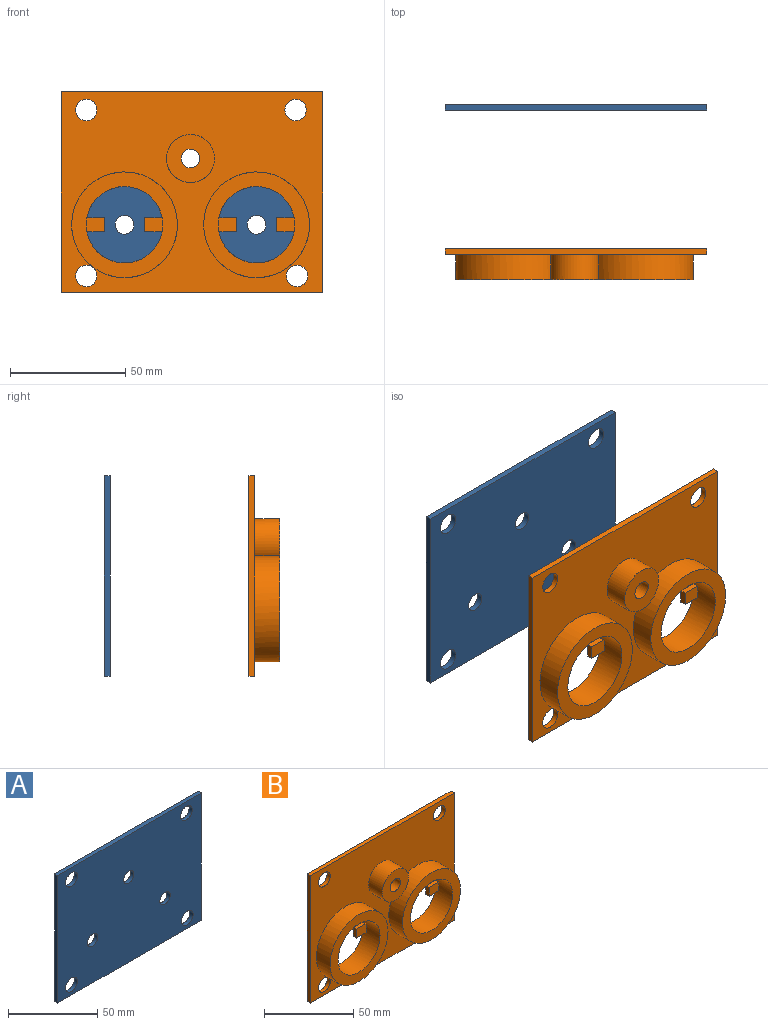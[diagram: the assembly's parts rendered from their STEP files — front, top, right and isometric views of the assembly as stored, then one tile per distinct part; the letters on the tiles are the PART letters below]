
ASSEMBLY  parts=2 mates=1
PART A: 13 faces, bbox 113.6x2.5x87.2 mm
  f0: plane 113.61x2.54mm, normal (0,0,-1), area 288.6mm2, adj f1,f10,f11,f12
  f1: plane 87.22x2.54mm, normal (1,0,0), area 221.5mm2, adj f0,f2,f11,f12
  f2: plane 113.61x2.54mm, normal (0,0,1), area 288.6mm2, adj f1,f10,f11,f12
  f3: cylinder r=4.65mm len=9.29mm, axis (0,1,0), area 74.1mm2, adj f11,f12
  f4: cylinder r=4.65mm len=9.29mm, axis (0,1,0), area 74.1mm2, adj f11,f12
  f5: cylinder r=4.65mm len=9.29mm, axis (0,1,0), area 74.1mm2, adj f11,f12
  f6: cylinder r=4.65mm len=9.29mm, axis (0,1,0), area 74.1mm2, adj f11,f12
  f7: cylinder r=4.07mm len=8.14mm, axis (0,1,0), area 65mm2, adj f11,f12
  f8: cylinder r=4.07mm len=8.14mm, axis (0,1,0), area 65mm2, adj f11,f12
  f9: cylinder r=4.07mm len=8.14mm, axis (0,1,0), area 65mm2, adj f11,f12
  f10: plane 87.22x2.54mm, normal (-1,0,0), area 221.5mm2, adj f0,f2,f11,f12
  f11: plane 113.61x87.22mm, normal (0,-1,0), area 9481.8mm2, adj f0,f1,f2,f3,f4,f5,f6,f7
  f12: plane 113.61x87.22mm, normal (0,1,0), area 9481.8mm2, adj f0,f1,f2,f3,f4,f5,f6,f7
PART B: 35 faces, bbox 113.6x13.3x87.2 mm
  f0: plane 113.61x2.54mm, normal (0,0,1), area 288.6mm2, adj f1,f5,f11,f12
  f1: plane 87.22x2.54mm, normal (-1,0,0), area 221.5mm2, adj f0,f2,f11,f12
  f2: plane 113.61x2.54mm, normal (0,0,-1), area 288.6mm2, adj f1,f5,f11,f12
  f3: cylinder r=4.07mm len=13.34mm, axis (0,1,0), area 341mm2, adj f12,f18
  f4: cylinder r=16.61mm len=33.23mm, axis (0,1,0), area 1360.9mm2, adj f12,f14,f27,f29,f30,f31,f33,f34
  f5: plane 87.22x2.54mm, normal (1,0,0), area 221.5mm2, adj f0,f2,f11,f12
  f6: cylinder r=4.65mm len=9.29mm, axis (0,1,0), area 74.1mm2, adj f11,f12
  f7: cylinder r=4.65mm len=9.29mm, axis (0,1,0), area 74.1mm2, adj f11,f12
  f8: cylinder r=4.65mm len=9.29mm, axis (0,1,0), area 74.1mm2, adj f11,f12
  f9: cylinder r=4.65mm len=9.29mm, axis (0,1,0), area 74.1mm2, adj f11,f12
  f10: cylinder r=16.61mm len=33.23mm, axis (0,1,0), area 1360.9mm2, adj f12,f16,f20,f21,f22,f23,f25,f26
  f11: plane 113.61x87.22mm, normal (0,-1,0), area 5983.5mm2, adj f0,f1,f2,f5,f6,f7,f8,f9
  f12: plane 113.61x87.22mm, normal (0,1,0), area 8038.4mm2, adj f0,f1,f2,f3,f4,f5,f6,f7
  f13: cylinder r=22.96mm len=45.93mm, axis (0,1,0), area 1557.6mm2, adj f11,f14
  f14: plane 45.93x45.93mm, normal (0,-1,0), area 789.5mm2, adj f4,f13
  f15: cylinder r=22.96mm len=45.93mm, axis (0,1,0), area 1557.6mm2, adj f11,f16
  f16: plane 45.93x45.93mm, normal (0,-1,0), area 789.5mm2, adj f10,f15
  f17: cylinder r=10.42mm len=20.84mm, axis (0,1,0), area 706.8mm2, adj f11,f18
  f18: plane 20.84x20.84mm, normal (0,-1,0), area 289.1mm2, adj f3,f17
  f19: plane 6.08x2.54mm, normal (1,0,0), area 15.5mm2, adj f12,f20,f21,f22
  f20: plane 7.49x2.54mm, normal (0,0,-1), area 19mm2, adj f10,f12,f19,f22
  f21: plane 7.49x2.54mm, normal (0,0,1), area 19mm2, adj f10,f12,f19,f22
  f22: plane 7.77x6.08mm, normal (0,-1,0), area 46.7mm2, adj f10,f19,f20,f21
  f23: plane 7.49x2.54mm, normal (0,0,-1), area 19mm2, adj f10,f12,f24,f26
  f24: plane 6.08x2.54mm, normal (-1,0,0), area 15.5mm2, adj f12,f23,f25,f26
  f25: plane 7.49x2.54mm, normal (0,0,1), area 19mm2, adj f10,f12,f24,f26
  f26: plane 7.77x6.08mm, normal (0,-1,0), area 46.7mm2, adj f10,f23,f24,f25
  f27: plane 7.49x2.54mm, normal (0,0,1), area 19mm2, adj f4,f12,f28,f30
  f28: plane 6.08x2.54mm, normal (1,0,0), area 15.5mm2, adj f12,f27,f29,f30
  f29: plane 7.49x2.54mm, normal (0,0,-1), area 19mm2, adj f4,f12,f28,f30
  f30: plane 7.77x6.08mm, normal (0,-1,0), area 46.7mm2, adj f4,f27,f28,f29
  f31: plane 7.49x2.54mm, normal (0,0,-1), area 19mm2, adj f4,f12,f32,f34
  f32: plane 6.08x2.54mm, normal (-1,0,0), area 15.5mm2, adj f12,f31,f33,f34
  f33: plane 7.49x2.54mm, normal (0,0,1), area 19mm2, adj f4,f12,f32,f34
  f34: plane 7.77x6.08mm, normal (0,-1,0), area 46.7mm2, adj f4,f31,f32,f33
PLACE A t=(-4.24,69.28,0.86)mm
PLACE B t=(-0.92,6.54,-14.19)mm fixed
MATE slider B.f6 <-> A.f3  axis (0,1,0) through (44.72,6.54,35.69)mm
